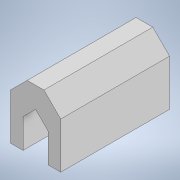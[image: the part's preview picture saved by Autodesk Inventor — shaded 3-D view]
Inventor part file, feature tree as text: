
AUTODESK INVENTOR PART (.ipt)
format: ipt  version: 2021 (Build 250183000, 183)  size: 96,768 bytes
history: native  units: in
note: dims shown in document units (in); Inventor stores cm internally (conversion verified against a paired STEP export)
features: extrude x1, sketch x1
ambient origin geometry x8: Origin, YZ Plane, XZ Plane, XY Plane, X Axis, Y Axis, Z Axis, Center Point
bodies: Solid1 (feature_tree)
feature tree (2):
  extrude  "Extrusion1"  Depth=1.0236in
  sketch  "Sketch1"  dims[d1=0.1181in d2=0.4331in d4=0.0787in d5=0.3937in d7=1.0236in d8=0.0in]
